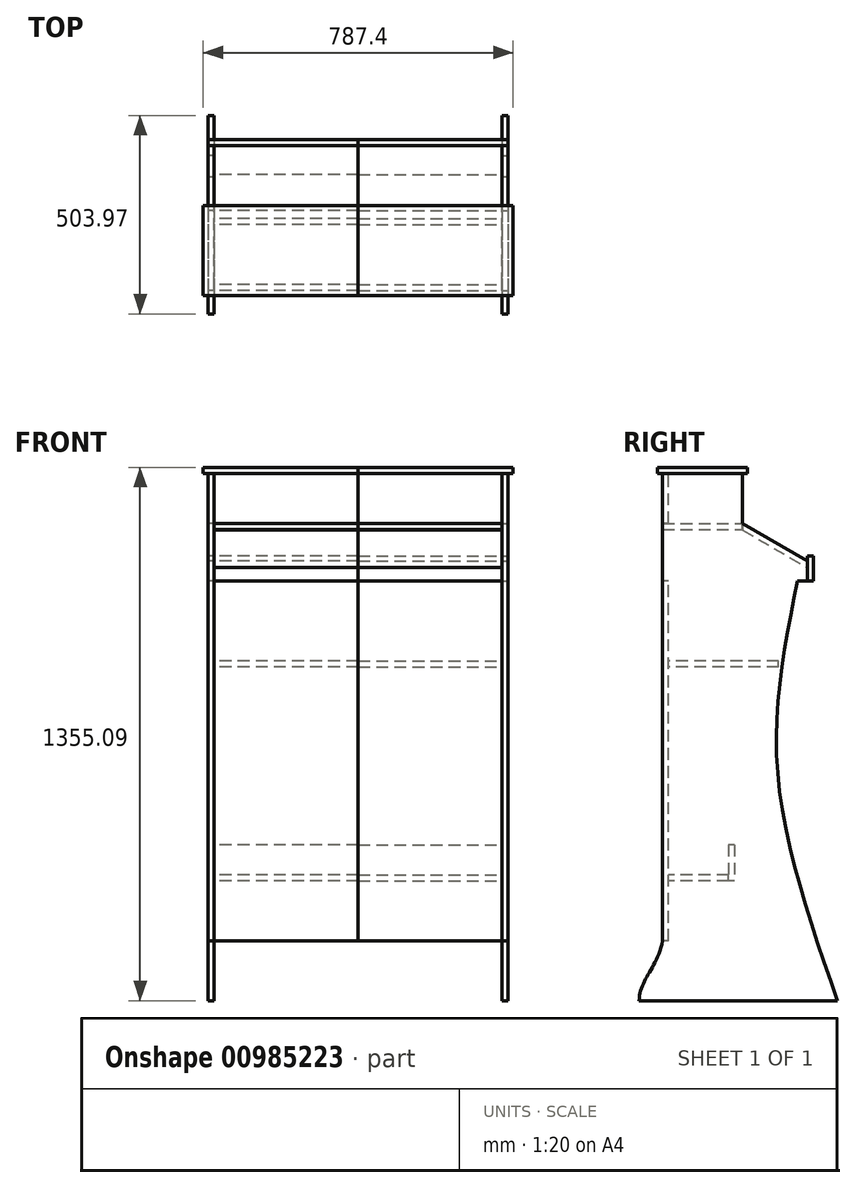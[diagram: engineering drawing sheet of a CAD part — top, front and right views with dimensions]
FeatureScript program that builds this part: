
annotation { "Feature Type Name" : "Feature", "Feature Type Description" : "" }
export const myFeature = defineFeature(function(context is Context, id is Id, definition is map)
    precondition{}
    {
        {
            var Q0;
            Q0=qCreatedBy(makeId("Right.planeOp"),FACE);
            cPlane(context, id + "F0", {"entities" : qUnion([Q0]), "cplaneType" : CPlaneType.OFFSET, "offset" : 381 * mm, "oppositeDirection" : true, "width" : 152.4 * mm, "height" : 152.4 * mm});
        }
        {
            var Q0;
            Q0=qCreatedBy(makeId("Right.planeOp"),FACE);
            var sketch = newSketch(context, id + "F1", { "sketchPlane" : qUnion([Q0])});
            skLineSegment(sketch, "E0", {"start": v(-2177.96, 1117.6) * mm, "end": v(2252.33, 1117.6) * mm, "construction": true});
            skLineSegment(sketch, "E1", {"start": v(0, 1117.6) * mm, "end": v(-1136.25, 1773.62) * mm, "construction": true});
            skLineSegment(sketch, "E2", {"start": v(-2442.64, 1339.85) * mm, "end": v(2338.35, 1339.85) * mm, "construction": true});
            skLineSegment(sketch, "E3", {"start": v(0, 1117.6) * mm, "end": v(-164.98, 1212.85) * mm});
            skLineSegment(sketch, "E4", {"start": v(-164.98, 1212.85) * mm, "end": v(-164.98, 1339.85) * mm});
            skLineSegment(sketch, "E5", {"start": v(-164.98, 1339.85) * mm, "end": v(-368.18, 1339.85) * mm});
            skLineSegment(sketch, "E6", {"start": v(-376.97, 0) * mm, "end": v(0, 0) * mm});
            skLineSegment(sketch, "E7", {"start": v(0, 1117.6) * mm, "end": v(0, 1066.8) * mm});
            skLineSegment(sketch, "E8", {"start": v(-76.08, 2024.83) * mm, "end": v(-76.08, -524.84) * mm, "construction": true});
            skPoint(sketch, "E9", {"position": v(-76.08, 584.2) * mm});
            skLineSegment(sketch, "E10", {"start": v(0, 1066.8) * mm, "end": v(-25.4, 1066.8) * mm});
            skLineSegment(sketch, "E11", {"start": v(-368.18, 1339.85) * mm, "end": v(-368.18, 152.15) * mm});
            skLineSegment(sketch, "E12", {"start": v(-376.97, 0) * mm, "end": v(-427.77, 0) * mm});
            skFitSpline(sketch, "E13", {"points": [v(-368.18, 152.15) * mm, v(-427.77, 0) * mm], "startDerivative": vector(-41.73, -208.76) * mm, "endDerivative": vector(-1.61, -155.59) * mm});
            skLineSegment(sketch, "E14", {"start": v(0, 0) * mm, "end": v(76.2, 0) * mm});
            skFitSpline(sketch, "E15", {"points": [v(-25.4, 1066.8) * mm, v(-76.08, 584.2) * mm, v(76.2, 0) * mm], "startDerivative": vector(-200.8, -1000.32) * mm, "endDerivative": vector(393.2, -1130.9) * mm});
            skSolve(sketch);
        }
        {
            var Q0;
            Q0=makeQuery(id+"F1.imprint","IMPRINT",FACE,{"disambiguationData":[TD([[makeQuery(id+"F1.imprint","IMPRINT",EDGE,{"derivedFrom":sQuery(id+"F1.wireOp",EDGE,"E3")}),1.0]])]});
            extrude(context, id + "F2", {"entities" : qUnion([Q0]), "oppositeDirection" : true, "depth" : 15.24 * mm, "offsetDistance" : 25.4 * mm});
        }
        {
            var Q0;
            Q0=qCreatedBy(makeId("Right.planeOp"),FACE);
            var sketch = newSketch(context, id + "F3", { "sketchPlane" : qUnion([Q0])});
            skLineSegment(sketch, "E16.0", {"start": v(0, 1117.6) * mm, "end": v(0, 1066.8) * mm});
            skLineSegment(sketch, "E17", {"start": v(0, 1117.6) * mm, "end": v(0, 1130.3) * mm});
            skLineSegment(sketch, "E18", {"start": v(0, 1130.3) * mm, "end": v(15.24, 1130.3) * mm});
            skLineSegment(sketch, "E19", {"start": v(15.24, 1130.3) * mm, "end": v(15.24, 1066.8) * mm});
            skLineSegment(sketch, "E20", {"start": v(15.24, 1066.8) * mm, "end": v(0, 1066.8) * mm});
            skSolve(sketch);
        }
        {
            var Q0;
            Q0=makeQuery(id+"F3.imprint","IMPRINT",FACE,{"disambiguationData":[TD([[makeQuery(id+"F3.imprint","IMPRINT",EDGE,{"derivedFrom":sQuery(id+"F3.wireOp",EDGE,"E16.0")}),1.0]])]});
            var Q1;
            Q1=qCreatedBy(id+"F0.planeOp",FACE);
            extrude(context, id + "F4", {"entities" : qUnion([Q0]), "endBound" : BoundingType.UP_TO_SURFACE, "oppositeDirection" : true, "depth" : 558.8 * mm, "endBoundEntityFace" : qUnion([Q1]), "offsetDistance" : 25.4 * mm});
        }
        {
            var Q0;
            Q0=makeQuery(id+"F2.opExtrude","CAP_FACE",FACE,{"disambiguationData":[OSD([sQuery(id+"F1.wireOp",EDGE,"E3"),sQuery(id+"F1.wireOp",EDGE,"E4"),sQuery(id+"F1.wireOp",EDGE,"E5"),sQuery(id+"F1.wireOp",EDGE,"E6"),sQuery(id+"F1.wireOp",EDGE,"E7"),sQuery(id+"F1.wireOp",EDGE,"E10"),sQuery(id+"F1.wireOp",EDGE,"E11"),sQuery(id+"F1.wireOp",EDGE,"E12"),sQuery(id+"F1.wireOp",EDGE,"E13"),sQuery(id+"F1.wireOp",EDGE,"E14"),sQuery(id+"F1.wireOp",EDGE,"E15")])],"isStart":false});
            var sketch = newSketch(context, id + "F5", { "sketchPlane" : qUnion([Q0])});
            skLineSegment(sketch, "E21.0", {"start": v(0, 1117.6) * mm, "end": v(164.98, 1212.85) * mm});
            skLineSegment(sketch, "E22", {"start": v(0, 1100) * mm, "end": v(164.98, 1195.25) * mm});
            skLineSegment(sketch, "E23", {"start": v(164.98, 1195.25) * mm, "end": v(164.98, 1212.85) * mm});
            skLineSegment(sketch, "E24", {"start": v(0, 1100) * mm, "end": v(0, 1117.6) * mm});
            skSolve(sketch);
        }
        {
            var Q0;
            Q0=makeQuery(id+"F5.imprint","IMPRINT",FACE,{"disambiguationData":[TD([[makeQuery(id+"F5.imprint","IMPRINT",EDGE,{"derivedFrom":sQuery(id+"F5.wireOp",EDGE,"E21.0")}),-1.0]])]});
            var Q1;
            Q1=qCreatedBy(id+"F0.planeOp",FACE);
            extrude(context, id + "F6", {"entities" : qUnion([Q0]), "endBound" : BoundingType.UP_TO_SURFACE, "depth" : 25.4 * mm, "endBoundEntityFace" : qUnion([Q1]), "offsetDistance" : 25.4 * mm});
        }
        {
            var Q0;
            Q0=makeQuery(id+"F2.opExtrude","CAP_FACE",FACE,{"disambiguationData":[OSD([sQuery(id+"F1.wireOp",EDGE,"E3"),sQuery(id+"F1.wireOp",EDGE,"E4"),sQuery(id+"F1.wireOp",EDGE,"E5"),sQuery(id+"F1.wireOp",EDGE,"E6"),sQuery(id+"F1.wireOp",EDGE,"E7"),sQuery(id+"F1.wireOp",EDGE,"E10"),sQuery(id+"F1.wireOp",EDGE,"E11"),sQuery(id+"F1.wireOp",EDGE,"E12"),sQuery(id+"F1.wireOp",EDGE,"E13"),sQuery(id+"F1.wireOp",EDGE,"E14"),sQuery(id+"F1.wireOp",EDGE,"E15")])],"isStart":false});
            var sketch = newSketch(context, id + "F7", { "sketchPlane" : qUnion([Q0])});
            skLineSegment(sketch, "E25.bottom", {"start": v(164.98, 1212.85) * mm, "end": v(368.18, 1212.85) * mm});
            skLineSegment(sketch, "E25.top", {"start": v(164.98, 1197.61) * mm, "end": v(368.18, 1197.61) * mm});
            skLineSegment(sketch, "E25.left", {"start": v(164.98, 1212.85) * mm, "end": v(164.98, 1197.61) * mm});
            skLineSegment(sketch, "E25.right", {"start": v(368.18, 1212.85) * mm, "end": v(368.18, 1197.61) * mm});
            skSolve(sketch);
        }
        {
            var Q0;
            Q0=makeQuery(id+"F7.imprint","IMPRINT",FACE,{"disambiguationData":[TD([[makeQuery(id+"F7.imprint","IMPRINT",EDGE,{"derivedFrom":sQuery(id+"F7.wireOp",EDGE,"E25.bottom")}),-1.0]])]});
            var Q1;
            Q1=qCreatedBy(id+"F0.planeOp",FACE);
            extrude(context, id + "F8", {"entities" : qUnion([Q0]), "endBound" : BoundingType.UP_TO_SURFACE, "depth" : 25.4 * mm, "endBoundEntityFace" : qUnion([Q1]), "offsetDistance" : 25.4 * mm});
        }
        {
            var Q0;
            Q0=makeQuery(id+"F2.opExtrude","CAP_FACE",FACE,{"disambiguationData":[OSD([sQuery(id+"F1.wireOp",EDGE,"E3"),sQuery(id+"F1.wireOp",EDGE,"E4"),sQuery(id+"F1.wireOp",EDGE,"E5"),sQuery(id+"F1.wireOp",EDGE,"E6"),sQuery(id+"F1.wireOp",EDGE,"E7"),sQuery(id+"F1.wireOp",EDGE,"E10"),sQuery(id+"F1.wireOp",EDGE,"E11"),sQuery(id+"F1.wireOp",EDGE,"E12"),sQuery(id+"F1.wireOp",EDGE,"E13"),sQuery(id+"F1.wireOp",EDGE,"E14"),sQuery(id+"F1.wireOp",EDGE,"E15")])],"isStart":false});
            var sketch = newSketch(context, id + "F9", { "sketchPlane" : qUnion([Q0])});
            skLineSegment(sketch, "E26.0", {"start": v(368.18, 1212.85) * mm, "end": v(164.98, 1212.85) * mm, "construction": true});
            skLineSegment(sketch, "E27.bottom", {"start": v(368.18, 1339.85) * mm, "end": v(352.94, 1339.85) * mm});
            skLineSegment(sketch, "E27.top", {"start": v(368.18, 1212.85) * mm, "end": v(352.94, 1212.85) * mm});
            skLineSegment(sketch, "E27.left", {"start": v(368.18, 1339.85) * mm, "end": v(368.18, 1212.85) * mm});
            skLineSegment(sketch, "E27.right", {"start": v(352.94, 1339.85) * mm, "end": v(352.94, 1212.85) * mm});
            skSolve(sketch);
        }
        {
            var Q0;
            Q0=makeQuery(id+"F9.imprint","IMPRINT",FACE,{"disambiguationData":[TD([[makeQuery(id+"F9.imprint","IMPRINT",EDGE,{"derivedFrom":sQuery(id+"F9.wireOp",EDGE,"E27.bottom")}),-1.0]])]});
            var Q1;
            Q1=qCreatedBy(id+"F0.planeOp",FACE);
            extrude(context, id + "F10", {"entities" : qUnion([Q0]), "endBound" : BoundingType.UP_TO_SURFACE, "depth" : 25.4 * mm, "endBoundEntityFace" : qUnion([Q1]), "offsetDistance" : 25.4 * mm});
        }
        {
            var Q0;
            Q0=makeQuery(id+"F2.opExtrude","CAP_FACE",FACE,{"disambiguationData":[OSD([sQuery(id+"F1.wireOp",EDGE,"E3"),sQuery(id+"F1.wireOp",EDGE,"E4"),sQuery(id+"F1.wireOp",EDGE,"E5"),sQuery(id+"F1.wireOp",EDGE,"E6"),sQuery(id+"F1.wireOp",EDGE,"E7"),sQuery(id+"F1.wireOp",EDGE,"E10"),sQuery(id+"F1.wireOp",EDGE,"E11"),sQuery(id+"F1.wireOp",EDGE,"E12"),sQuery(id+"F1.wireOp",EDGE,"E13"),sQuery(id+"F1.wireOp",EDGE,"E14"),sQuery(id+"F1.wireOp",EDGE,"E15")])],"isStart":true});
            var sketch = newSketch(context, id + "F11", { "sketchPlane" : qUnion([Q0])});
            skLineSegment(sketch, "E28.0", {"start": v(-164.98, 1339.85) * mm, "end": v(-368.18, 1339.85) * mm, "construction": true});
            skLineSegment(sketch, "E29.bottom", {"start": v(-380.88, 1339.85) * mm, "end": v(-152.28, 1339.85) * mm});
            skLineSegment(sketch, "E29.top", {"start": v(-380.88, 1355.1) * mm, "end": v(-152.28, 1355.1) * mm});
            skLineSegment(sketch, "E29.left", {"start": v(-380.88, 1339.85) * mm, "end": v(-380.88, 1355.1) * mm});
            skLineSegment(sketch, "E29.right", {"start": v(-152.28, 1339.85) * mm, "end": v(-152.28, 1355.1) * mm});
            skSolve(sketch);
        }
        {
            var Q0;
            Q0=makeQuery(id+"F11.imprint","IMPRINT",FACE,{"disambiguationData":[TD([[makeQuery(id+"F11.imprint","IMPRINT",EDGE,{"derivedFrom":sQuery(id+"F11.wireOp",EDGE,"E29.top")}),-1.0]])]});
            var Q1;
            Q1=qCreatedBy(id+"F0.planeOp",FACE);
            extrude(context, id + "F12", {"entities" : qUnion([Q0]), "endBound" : BoundingType.UP_TO_SURFACE, "oppositeDirection" : true, "depth" : 25.4 * mm, "endBoundEntityFace" : qUnion([Q1]), "offsetDistance" : 25.4 * mm, "hasSecondDirection" : true, "secondDirectionOppositeDirection" : false, "secondDirectionDepth" : 12.7 * mm});
        }
        {
            var Q0;
            Q0=makeQuery(id+"F2.opExtrude","CAP_FACE",FACE,{"disambiguationData":[OSD([sQuery(id+"F1.wireOp",EDGE,"E3"),sQuery(id+"F1.wireOp",EDGE,"E4"),sQuery(id+"F1.wireOp",EDGE,"E5"),sQuery(id+"F1.wireOp",EDGE,"E6"),sQuery(id+"F1.wireOp",EDGE,"E7"),sQuery(id+"F1.wireOp",EDGE,"E10"),sQuery(id+"F1.wireOp",EDGE,"E11"),sQuery(id+"F1.wireOp",EDGE,"E12"),sQuery(id+"F1.wireOp",EDGE,"E13"),sQuery(id+"F1.wireOp",EDGE,"E14"),sQuery(id+"F1.wireOp",EDGE,"E15")])],"isStart":false});
            var sketch = newSketch(context, id + "F13", { "sketchPlane" : qUnion([Q0])});
            skLineSegment(sketch, "E30.bottom", {"start": v(368.18, 1066.8) * mm, "end": v(352.94, 1066.8) * mm});
            skLineSegment(sketch, "E30.top", {"start": v(368.18, 152.15) * mm, "end": v(352.94, 152.15) * mm});
            skLineSegment(sketch, "E30.left", {"start": v(368.18, 1066.8) * mm, "end": v(368.18, 152.15) * mm});
            skLineSegment(sketch, "E30.right", {"start": v(352.94, 1066.8) * mm, "end": v(352.94, 152.15) * mm});
            skSolve(sketch);
        }
        {
            var Q0;
            Q0=makeQuery(id+"F13.imprint","IMPRINT",FACE,{"disambiguationData":[TD([[makeQuery(id+"F13.imprint","IMPRINT",EDGE,{"derivedFrom":sQuery(id+"F13.wireOp",EDGE,"E30.bottom")}),1.0]])]});
            var Q1;
            Q1=qCreatedBy(id+"F0.planeOp",FACE);
            extrude(context, id + "F14", {"entities" : qUnion([Q0]), "endBound" : BoundingType.UP_TO_SURFACE, "depth" : 25.4 * mm, "endBoundEntityFace" : qUnion([Q1]), "offsetDistance" : 25.4 * mm});
        }
        {
            var Q0;
            Q0=makeQuery(id+"F2.opExtrude","CAP_FACE",FACE,{"disambiguationData":[OSD([sQuery(id+"F1.wireOp",EDGE,"E3"),sQuery(id+"F1.wireOp",EDGE,"E4"),sQuery(id+"F1.wireOp",EDGE,"E5"),sQuery(id+"F1.wireOp",EDGE,"E6"),sQuery(id+"F1.wireOp",EDGE,"E7"),sQuery(id+"F1.wireOp",EDGE,"E10"),sQuery(id+"F1.wireOp",EDGE,"E11"),sQuery(id+"F1.wireOp",EDGE,"E12"),sQuery(id+"F1.wireOp",EDGE,"E13"),sQuery(id+"F1.wireOp",EDGE,"E14"),sQuery(id+"F1.wireOp",EDGE,"E15")])],"isStart":false});
            var sketch = newSketch(context, id + "F15", { "sketchPlane" : qUnion([Q0])});
            skLineSegment(sketch, "E31", {"start": v(0, 863.6) * mm, "end": v(587.47, 863.6) * mm, "construction": true});
            skLineSegment(sketch, "E32.0", {"start": v(352.94, 152.15) * mm, "end": v(352.94, 1066.8) * mm, "construction": true});
            skLineSegment(sketch, "E33.bottom", {"start": v(352.94, 863.6) * mm, "end": v(73.54, 863.6) * mm});
            skLineSegment(sketch, "E33.top", {"start": v(352.94, 848.36) * mm, "end": v(73.54, 848.36) * mm});
            skLineSegment(sketch, "E33.left", {"start": v(352.94, 863.6) * mm, "end": v(352.94, 848.36) * mm});
            skLineSegment(sketch, "E33.right", {"start": v(73.54, 863.6) * mm, "end": v(73.54, 848.36) * mm});
            skSolve(sketch);
        }
        {
            var Q0;
            Q0=makeQuery(id+"F15.imprint","IMPRINT",FACE,{"disambiguationData":[TD([[makeQuery(id+"F15.imprint","IMPRINT",EDGE,{"derivedFrom":sQuery(id+"F15.wireOp",EDGE,"E33.bottom")}),1.0]])]});
            var Q1;
            Q1=qCreatedBy(id+"F0.planeOp",FACE);
            extrude(context, id + "F16", {"entities" : qUnion([Q0]), "endBound" : BoundingType.UP_TO_SURFACE, "depth" : 25.4 * mm, "endBoundEntityFace" : qUnion([Q1]), "offsetDistance" : 25.4 * mm});
        }
        {
            var Q0;
            Q0=makeQuery(id+"F2.opExtrude","CAP_FACE",FACE,{"disambiguationData":[OSD([sQuery(id+"F1.wireOp",EDGE,"E3"),sQuery(id+"F1.wireOp",EDGE,"E4"),sQuery(id+"F1.wireOp",EDGE,"E5"),sQuery(id+"F1.wireOp",EDGE,"E6"),sQuery(id+"F1.wireOp",EDGE,"E7"),sQuery(id+"F1.wireOp",EDGE,"E10"),sQuery(id+"F1.wireOp",EDGE,"E11"),sQuery(id+"F1.wireOp",EDGE,"E12"),sQuery(id+"F1.wireOp",EDGE,"E13"),sQuery(id+"F1.wireOp",EDGE,"E14"),sQuery(id+"F1.wireOp",EDGE,"E15")])],"isStart":false});
            var sketch = newSketch(context, id + "F17", { "sketchPlane" : qUnion([Q0])});
            skLineSegment(sketch, "E34.0", {"start": v(352.94, 152.15) * mm, "end": v(352.94, 1066.8) * mm, "construction": true});
            skLineSegment(sketch, "E35.bottom", {"start": v(352.94, 320.04) * mm, "end": v(200.54, 320.04) * mm});
            skLineSegment(sketch, "E35.top", {"start": v(352.94, 304.8) * mm, "end": v(200.54, 304.8) * mm});
            skLineSegment(sketch, "E35.left", {"start": v(352.94, 320.04) * mm, "end": v(352.94, 304.8) * mm});
            skLineSegment(sketch, "E35.right", {"start": v(200.54, 320.04) * mm, "end": v(200.54, 304.8) * mm});
            skSolve(sketch);
        }
        {
            var Q0;
            Q0=makeQuery(id+"F17.imprint","IMPRINT",FACE,{"disambiguationData":[TD([[makeQuery(id+"F17.imprint","IMPRINT",EDGE,{"derivedFrom":sQuery(id+"F17.wireOp",EDGE,"E35.bottom")}),1.0]])]});
            var Q1;
            Q1=qCreatedBy(id+"F0.planeOp",FACE);
            extrude(context, id + "F18", {"entities" : qUnion([Q0]), "endBound" : BoundingType.UP_TO_SURFACE, "depth" : 25.4 * mm, "endBoundEntityFace" : qUnion([Q1]), "offsetDistance" : 25.4 * mm});
        }
        {
            var Q0;
            Q0=makeQuery(id+"F2.opExtrude","CAP_FACE",FACE,{"disambiguationData":[OSD([sQuery(id+"F1.wireOp",EDGE,"E3"),sQuery(id+"F1.wireOp",EDGE,"E4"),sQuery(id+"F1.wireOp",EDGE,"E5"),sQuery(id+"F1.wireOp",EDGE,"E6"),sQuery(id+"F1.wireOp",EDGE,"E7"),sQuery(id+"F1.wireOp",EDGE,"E10"),sQuery(id+"F1.wireOp",EDGE,"E11"),sQuery(id+"F1.wireOp",EDGE,"E12"),sQuery(id+"F1.wireOp",EDGE,"E13"),sQuery(id+"F1.wireOp",EDGE,"E14"),sQuery(id+"F1.wireOp",EDGE,"E15")])],"isStart":false});
            var sketch = newSketch(context, id + "F19", { "sketchPlane" : qUnion([Q0])});
            skLineSegment(sketch, "E36.0", {"start": v(200.54, 304.8) * mm, "end": v(200.54, 320.04) * mm, "construction": true});
            skLineSegment(sketch, "E37.bottom", {"start": v(200.54, 304.8) * mm, "end": v(185.3, 304.8) * mm});
            skLineSegment(sketch, "E37.top", {"start": v(200.54, 396.24) * mm, "end": v(185.3, 396.24) * mm});
            skLineSegment(sketch, "E37.left", {"start": v(200.54, 304.8) * mm, "end": v(200.54, 396.24) * mm});
            skLineSegment(sketch, "E37.right", {"start": v(185.3, 304.8) * mm, "end": v(185.3, 396.24) * mm});
            skSolve(sketch);
        }
        {
            var Q0;
            Q0=makeQuery(id+"F19.imprint","IMPRINT",FACE,{"disambiguationData":[TD([[makeQuery(id+"F19.imprint","IMPRINT",EDGE,{"derivedFrom":sQuery(id+"F19.wireOp",EDGE,"E37.bottom")}),-1.0]])]});
            var Q1;
            Q1=qCreatedBy(id+"F0.planeOp",FACE);
            extrude(context, id + "F20", {"entities" : qUnion([Q0]), "endBound" : BoundingType.UP_TO_SURFACE, "depth" : 25.4 * mm, "endBoundEntityFace" : qUnion([Q1]), "offsetDistance" : 25.4 * mm});
        }
        {
            var Q0;
            Q0=makeQuery(id+"F4.opExtrude","SWEPT_BODY",BODY,{"disambiguationData":[OSD([sQuery(id+"F3.wireOp",EDGE,"E16.0"),sQuery(id+"F3.wireOp",EDGE,"E17"),sQuery(id+"F3.wireOp",EDGE,"E18"),sQuery(id+"F3.wireOp",EDGE,"E19"),sQuery(id+"F3.wireOp",EDGE,"E20")])]});
            var Q1;
            Q1=makeQuery(id+"F6.opExtrude","SWEPT_BODY",BODY,{"disambiguationData":[OSD([sQuery(id+"F5.wireOp",EDGE,"E21.0"),sQuery(id+"F5.wireOp",EDGE,"E22"),sQuery(id+"F5.wireOp",EDGE,"E23"),sQuery(id+"F5.wireOp",EDGE,"E24")])]});
            var Q2;
            Q2=makeQuery(id+"F8.opExtrude","SWEPT_BODY",BODY,{"disambiguationData":[OSD([sQuery(id+"F7.wireOp",EDGE,"E25.bottom"),sQuery(id+"F7.wireOp",EDGE,"E25.top"),sQuery(id+"F7.wireOp",EDGE,"E25.left"),sQuery(id+"F7.wireOp",EDGE,"E25.right")])]});
            var Q3;
            Q3=makeQuery(id+"F10.opExtrude","SWEPT_BODY",BODY,{"disambiguationData":[OSD([sQuery(id+"F9.wireOp",EDGE,"E27.bottom"),sQuery(id+"F9.wireOp",EDGE,"E27.top"),sQuery(id+"F9.wireOp",EDGE,"E27.left"),sQuery(id+"F9.wireOp",EDGE,"E27.right")])]});
            var Q4;
            Q4=makeQuery(id+"F12.opExtrude","SWEPT_BODY",BODY,{"disambiguationData":[OSD([sQuery(id+"F11.wireOp",EDGE,"E29.bottom"),sQuery(id+"F11.wireOp",EDGE,"E29.top"),sQuery(id+"F11.wireOp",EDGE,"E29.left"),sQuery(id+"F11.wireOp",EDGE,"E29.right")])]});
            var Q5;
            Q5=makeQuery(id+"F14.opExtrude","SWEPT_BODY",BODY,{"disambiguationData":[OSD([sQuery(id+"F13.wireOp",EDGE,"E30.bottom"),sQuery(id+"F13.wireOp",EDGE,"E30.top"),sQuery(id+"F13.wireOp",EDGE,"E30.left"),sQuery(id+"F13.wireOp",EDGE,"E30.right")])]});
            var Q6;
            Q6=makeQuery(id+"F16.opExtrude","SWEPT_BODY",BODY,{"disambiguationData":[OSD([sQuery(id+"F15.wireOp",EDGE,"E33.bottom"),sQuery(id+"F15.wireOp",EDGE,"E33.top"),sQuery(id+"F15.wireOp",EDGE,"E33.left"),sQuery(id+"F15.wireOp",EDGE,"E33.right")])]});
            var Q7;
            Q7=makeQuery(id+"F18.opExtrude","SWEPT_BODY",BODY,{"disambiguationData":[OSD([sQuery(id+"F17.wireOp",EDGE,"E35.bottom"),sQuery(id+"F17.wireOp",EDGE,"E35.top"),sQuery(id+"F17.wireOp",EDGE,"E35.left"),sQuery(id+"F17.wireOp",EDGE,"E35.right")])]});
            var Q8;
            Q8=makeQuery(id+"F20.opExtrude","SWEPT_BODY",BODY,{"disambiguationData":[OSD([sQuery(id+"F19.wireOp",EDGE,"E37.bottom"),sQuery(id+"F19.wireOp",EDGE,"E37.top"),sQuery(id+"F19.wireOp",EDGE,"E37.left"),sQuery(id+"F19.wireOp",EDGE,"E37.right")])]});
            var Q9;
            Q9=makeQuery(id+"F2.opExtrude","SWEPT_BODY",BODY,{"disambiguationData":[OSD([sQuery(id+"F1.wireOp",EDGE,"E3"),sQuery(id+"F1.wireOp",EDGE,"E4"),sQuery(id+"F1.wireOp",EDGE,"E5"),sQuery(id+"F1.wireOp",EDGE,"E6"),sQuery(id+"F1.wireOp",EDGE,"E7"),sQuery(id+"F1.wireOp",EDGE,"E10"),sQuery(id+"F1.wireOp",EDGE,"E11"),sQuery(id+"F1.wireOp",EDGE,"E12"),sQuery(id+"F1.wireOp",EDGE,"E13"),sQuery(id+"F1.wireOp",EDGE,"E14"),sQuery(id+"F1.wireOp",EDGE,"E15")])]});
            var Q10;
            Q10=qCreatedBy(id+"F0.planeOp",FACE);
            mirror(context, id + "F21", {"entities" : qUnion([Q0, Q1, Q2, Q3, Q4, Q5, Q6, Q7, Q8, Q9]), "mirrorPlane" : qUnion([Q10])});
        }
    });
